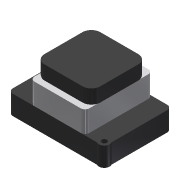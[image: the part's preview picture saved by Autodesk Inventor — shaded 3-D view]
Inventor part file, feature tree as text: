
AUTODESK INVENTOR PART (.ipt)
format: ipt  version: 2013 (Build 170138000, 138)  size: 143,360 bytes
history: native  units: in
note: dims shown in document units (in); Inventor stores cm internally (conversion verified against a paired STEP export)
features: extrude x3, sketch x3, fillet x2
ambient origin geometry x8: Origin, YZ Plane, XZ Plane, XY Plane, X Axis, Y Axis, Z Axis, Center Point
bodies: Solid1 (feature_tree), Solid2 (feature_tree), Solid3 (feature_tree)
feature tree (8):
  extrude  "Extrusion1"  Depth=1.547in
  extrude  "Extrusion2"  Depth=0.125in
  fillet  "Fillet1"  Radius=1.57in
  extrude  "Extrusion3"  Depth=0.3937in TaperAngle=0.0deg
  fillet  "Fillet2"  Radius=0.25in
  sketch  "Sketch2"  dims[d0=0.544in d1=0.0in d2=1.547in]
  sketch  "Sketch3"  dims[d4=0.6in d5=0.0in d6=0.125in d7=1.57in]
  sketch  "Sketch4"  dims[d8=1.57in d9=0.3937in d10=0.0in d11=0.25in]
